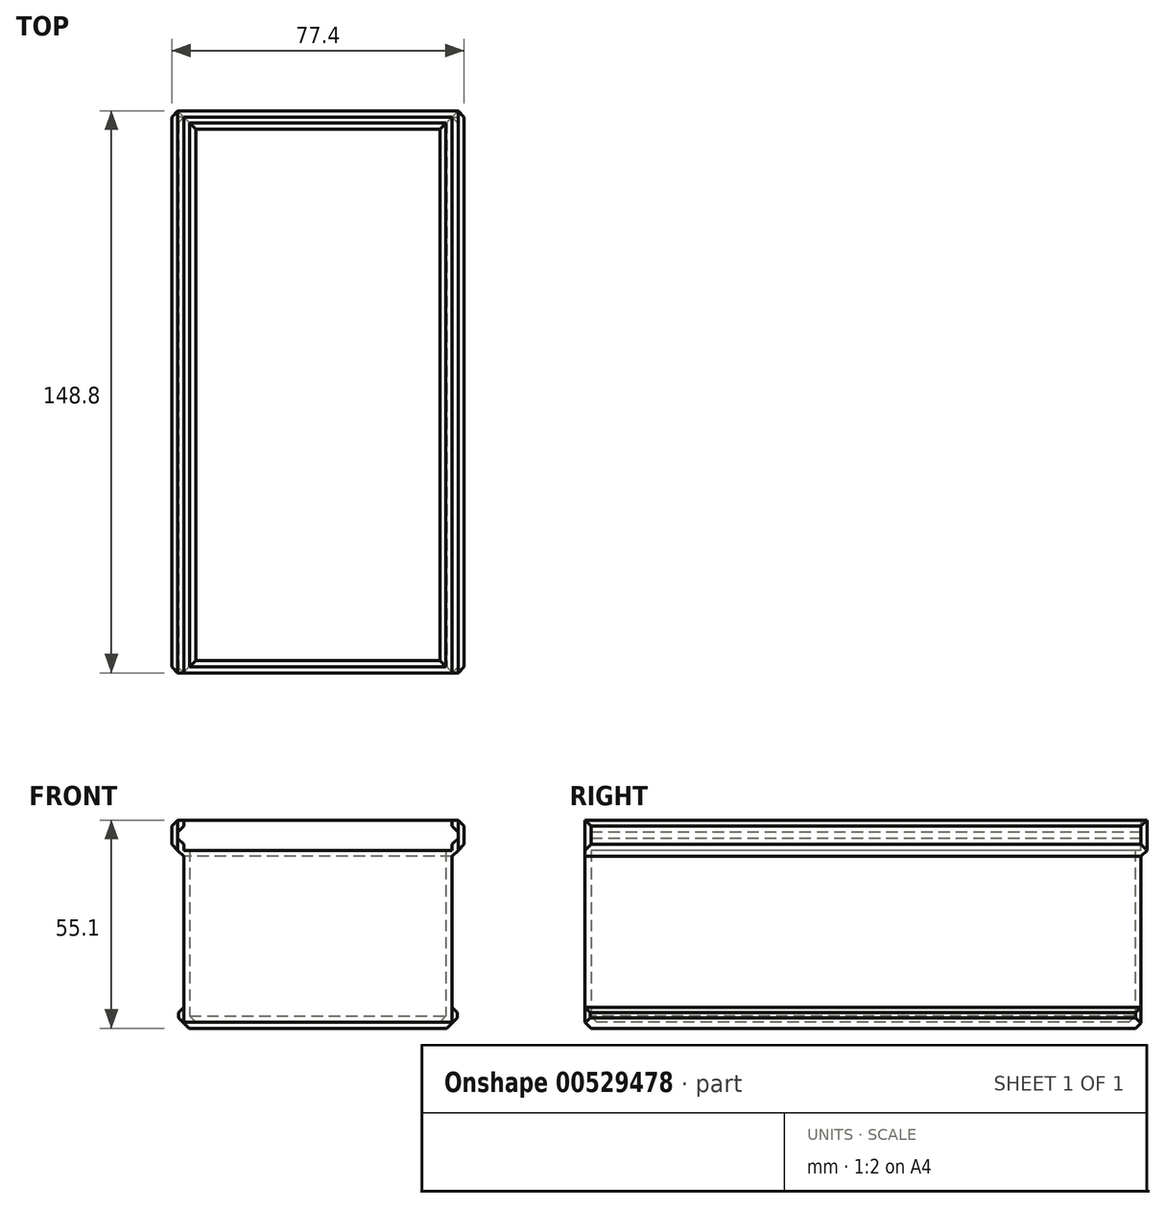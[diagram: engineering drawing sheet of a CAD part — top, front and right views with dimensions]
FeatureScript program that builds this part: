
annotation { "Feature Type Name" : "Feature", "Feature Type Description" : "" }
export const myFeature = defineFeature(function(context is Context, id is Id, definition is map)
    precondition{}
    {
        {
            assignVariable(context, id + "F0", {"name" : "width", "anyValue" : 41.5});
        }
        {
            assignVariable(context, id + "F1", {"name" : "thick", "anyValue" : 1.6});
        }
        {
            assignVariable(context, id + "F2", {"name" : "space", "anyValue" : 4});
        }
        {
            var Q0;
            Q0=qCreatedBy(makeId("Top.planeOp"),FACE);
            var sketch = newSketch(context, id + "F3", { "sketchPlane" : qUnion([Q0])});
            skLineSegment(sketch, "E0.bottom", {"start": v(33.9, 72) * mm, "end": v(-33.9, 72) * mm});
            skLineSegment(sketch, "E0.top", {"start": v(33.9, -72) * mm, "end": v(-33.9, -72) * mm});
            skLineSegment(sketch, "E0.left", {"start": v(33.9, 72) * mm, "end": v(33.9, -72) * mm});
            skLineSegment(sketch, "E0.right", {"start": v(-33.9, 72) * mm, "end": v(-33.9, -72) * mm});
            skPoint(sketch, "E0.middle", {"position": v(0, 0) * mm});
            skSolve(sketch);
        }
        {
            var Q0;
            Q0 = qSketchRegion(id + "F3", true);
            extrude(context, id + "F4", {"entities" : qUnion([Q0]), "depth" : (getVariable(context, 'width') + getVariable(context, 'space')) * mm, "offsetDistance" : 25 * mm});
        }
        {
            var Q0;
            Q0=makeQuery(id+"F4.opExtrude","CAP_FACE",FACE,{"disambiguationData":[OSD([sQuery(id+"F3.wireOp",EDGE,"E0.bottom"),sQuery(id+"F3.wireOp",EDGE,"E0.top"),sQuery(id+"F3.wireOp",EDGE,"E0.left"),sQuery(id+"F3.wireOp",EDGE,"E0.right")])],"isStart":false});
            shell(context, id + "F5", {"entities" : qUnion([Q0]), "thickness" : (getVariable(context, 'thick')) * mm, "oppositeDirection" : true});
        }
        {
            var Q0;
            Q0=makeQuery(id+"F4.opExtrude","SWEPT_FACE",FACE,{"disambiguationData":[OSD([sQuery(id+"F3.wireOp",EDGE,"E0.top")])]});
            var sketch = newSketch(context, id + "F6", { "sketchPlane" : qUnion([Q0])});
            skLineSegment(sketch, "E1", {"start": v(-37.1, 48.7) * mm, "end": v(-37.1, 50.3) * mm});
            skLineSegment(sketch, "E2", {"start": v(-37.1, 50.3) * mm, "end": v(-35.5, 51.9) * mm});
            skLineSegment(sketch, "E3", {"start": v(-35.5, 51.9) * mm, "end": v(-35.5, 53.5) * mm});
            skLineSegment(sketch, "E4", {"start": v(-37.1, 53.5) * mm, "end": v(-38.7, 51.9) * mm});
            skLineSegment(sketch, "E5", {"start": v(-38.7, 51.9) * mm, "end": v(-38.7, 47.1) * mm});
            skLineSegment(sketch, "E6", {"start": v(-37.1, 48.7) * mm, "end": v(-35.5, 47.1) * mm});
            skLineSegment(sketch, "E7", {"start": v(-35.5, 43.9) * mm, "end": v(-38.7, 47.1) * mm});
            skLineSegment(sketch, "E8", {"start": v(-37.1, 53.5) * mm, "end": v(-35.5, 53.5) * mm});
            skLineSegment(sketch, "E9", {"start": v(-35.5, 47.1) * mm, "end": v(-35.5, 45.5) * mm});
            skLineSegment(sketch, "E10", {"start": v(-35.5, 45.5) * mm, "end": v(-35.5, 43.9) * mm});
            skLineSegment(sketch, "E11.MirrorCS", {"start": v(37.1, 50.3) * mm, "end": v(35.5, 51.9) * mm});
            skLineSegment(sketch, "E12.MirrorCS", {"start": v(37.1, 53.5) * mm, "end": v(38.7, 51.9) * mm});
            skLineSegment(sketch, "E13.MirrorCS", {"start": v(35.5, 51.9) * mm, "end": v(35.5, 53.5) * mm});
            skLineSegment(sketch, "E14.MirrorCS", {"start": v(37.1, 48.7) * mm, "end": v(35.5, 47.1) * mm});
            skLineSegment(sketch, "E15.MirrorCS", {"start": v(35.5, 47.1) * mm, "end": v(35.5, 45.5) * mm});
            skLineSegment(sketch, "E16.MirrorCS", {"start": v(37.1, 53.5) * mm, "end": v(35.5, 53.5) * mm});
            skLineSegment(sketch, "E17.MirrorCS", {"start": v(35.5, 45.5) * mm, "end": v(35.5, 43.9) * mm});
            skLineSegment(sketch, "E18.MirrorCS", {"start": v(37.1, 48.7) * mm, "end": v(37.1, 50.3) * mm});
            skLineSegment(sketch, "E19.MirrorCS", {"start": v(38.7, 51.9) * mm, "end": v(38.7, 47.1) * mm});
            skLineSegment(sketch, "E20.MirrorCS", {"start": v(35.5, 43.9) * mm, "end": v(38.7, 47.1) * mm});
            skSolve(sketch);
        }
        {
            var Q0;
            Q0=makeQuery(id+"F6.imprint","IMPRINT",FACE,{"disambiguationData":[TD([[makeQuery(id+"F6.imprint","IMPRINT",EDGE,{"derivedFrom":sQuery(id+"F6.wireOp",EDGE,"E1")}),1.0]])]});
            var Q1;
            Q1=makeQuery(id+"F6.imprint","IMPRINT",FACE,{"disambiguationData":[TD([[makeQuery(id+"F6.imprint","IMPRINT",EDGE,{"derivedFrom":sQuery(id+"F6.wireOp",EDGE,"E11.MirrorCS")}),-1.0]])]});
            var Q2;
            Q2=makeQuery(id+"F4.opExtrude","SWEPT_FACE",FACE,{"disambiguationData":[OSD([sQuery(id+"F3.wireOp",EDGE,"E0.bottom")])]});
            extrude(context, id + "F7", {"entities" : qUnion([Q0, Q1]), "operationType" : NewBodyOperationType.ADD, "endBound" : BoundingType.UP_TO_SURFACE, "oppositeDirection" : true, "depth" : 25 * mm, "endBoundEntityFace" : qUnion([Q2]), "offsetDistance" : 25 * mm});
        }
        {
            var Q0;
            Q0=makeQuery(id+"F4.opExtrude","SWEPT_FACE",FACE,{"disambiguationData":[OSD([sQuery(id+"F3.wireOp",EDGE,"E0.top")])]});
            var sketch = newSketch(context, id + "F8", { "sketchPlane" : qUnion([Q0])});
            skLineSegment(sketch, "E21", {"start": v(-35.5, -0.2) * mm, "end": v(-36.9, 1.2) * mm});
            skLineSegment(sketch, "E22", {"start": v(-36.9, 1.2) * mm, "end": v(-36.9, 2.6) * mm});
            skLineSegment(sketch, "E23", {"start": v(-36.9, 2.6) * mm, "end": v(-35.5, 4) * mm});
            skLineSegment(sketch, "E24.MirrorCS", {"start": v(36.9, 2.6) * mm, "end": v(35.5, 4) * mm});
            skLineSegment(sketch, "E25.MirrorCS", {"start": v(36.9, 1.2) * mm, "end": v(36.9, 2.6) * mm});
            skLineSegment(sketch, "E26.MirrorCS", {"start": v(35.5, -0.2) * mm, "end": v(36.9, 1.2) * mm});
            skLineSegment(sketch, "E27", {"start": v(-35.5, 4) * mm, "end": v(-35.5, -0.2) * mm});
            skLineSegment(sketch, "E28.MirrorCS", {"start": v(35.5, 4) * mm, "end": v(35.5, -0.2) * mm});
            skSolve(sketch);
        }
        {
            var Q0;
            Q0=makeQuery(id+"F8.imprint","IMPRINT",FACE,{"disambiguationData":[TD([[makeQuery(id+"F8.imprint","IMPRINT",EDGE,{"derivedFrom":sQuery(id+"F8.wireOp",EDGE,"E21")}),-1.0]])]});
            var Q1;
            Q1=makeQuery(id+"F8.imprint","IMPRINT",FACE,{"disambiguationData":[TD([[makeQuery(id+"F8.imprint","IMPRINT",EDGE,{"derivedFrom":sQuery(id+"F8.wireOp",EDGE,"E24.MirrorCS")}),1.0]])]});
            var Q2;
            Q2=makeQuery(id+"F7.boolean.opBoolean","MERGE",FACE,{"derivedFrom":[makeQuery(id+"F4.opExtrude","SWEPT_FACE",FACE,{"disambiguationData":[OSD([sQuery(id+"F3.wireOp",EDGE,"E0.bottom")])]}),makeQuery(id+"F7.opExtrude","CAP_FACE",FACE,{"disambiguationData":[OSD([sQuery(id+"F6.wireOp",EDGE,"E1"),sQuery(id+"F6.wireOp",EDGE,"E2"),sQuery(id+"F6.wireOp",EDGE,"E3"),sQuery(id+"F6.wireOp",EDGE,"E4"),sQuery(id+"F6.wireOp",EDGE,"E5"),sQuery(id+"F6.wireOp",EDGE,"E6"),sQuery(id+"F6.wireOp",EDGE,"E7"),sQuery(id+"F6.wireOp",EDGE,"E8"),sQuery(id+"F6.wireOp",EDGE,"E9"),sQuery(id+"F6.wireOp",EDGE,"E10")])],"isStart":false}),makeQuery(id+"F7.opExtrude","CAP_FACE",FACE,{"disambiguationData":[OSD([sQuery(id+"F6.wireOp",EDGE,"E11.MirrorCS"),sQuery(id+"F6.wireOp",EDGE,"E12.MirrorCS"),sQuery(id+"F6.wireOp",EDGE,"E13.MirrorCS"),sQuery(id+"F6.wireOp",EDGE,"E14.MirrorCS"),sQuery(id+"F6.wireOp",EDGE,"E15.MirrorCS"),sQuery(id+"F6.wireOp",EDGE,"E16.MirrorCS"),sQuery(id+"F6.wireOp",EDGE,"E17.MirrorCS"),sQuery(id+"F6.wireOp",EDGE,"E18.MirrorCS"),sQuery(id+"F6.wireOp",EDGE,"E19.MirrorCS"),sQuery(id+"F6.wireOp",EDGE,"E20.MirrorCS")])],"isStart":false})]});
            extrude(context, id + "F9", {"entities" : qUnion([Q0, Q1]), "operationType" : NewBodyOperationType.ADD, "endBound" : BoundingType.UP_TO_SURFACE, "oppositeDirection" : true, "depth" : 25 * mm, "endBoundEntityFace" : qUnion([Q2]), "offsetDistance" : .4 * mm});
        }
        {
            var Q0;
            Q0=makeQuery(id+"F4.opExtrude","CAP_EDGE",EDGE,{"disambiguationData":[OSD([sQuery(id+"F3.wireOp",EDGE,"E0.right")])],"isStart":false});
            var Q1;
            Q1=makeQuery(id+"F4.opExtrude","CAP_EDGE",EDGE,{"disambiguationData":[OSD([sQuery(id+"F3.wireOp",EDGE,"E0.left")])],"isStart":false});
            var Q2;
            {var subQ0=sQuery(id+"F3.wireOp",EDGE,"E0.right");Q2=makeQuery(id+"F5.opShell","OFFSET_EDGE",EDGE,{"disambiguationData":[OSD([subQ0]),TDD([makeQuery(id+"F4.opExtrude","CAP_EDGE",EDGE,{"disambiguationData":[OSD([subQ0])],"isStart":true})])]});}
            var Q3;
            {var subQ0=sQuery(id+"F3.wireOp",EDGE,"E0.left");Q3=makeQuery(id+"F5.opShell","OFFSET_EDGE",EDGE,{"disambiguationData":[OSD([subQ0]),TDD([makeQuery(id+"F4.opExtrude","CAP_EDGE",EDGE,{"disambiguationData":[OSD([subQ0])],"isStart":true})])]});}
            var Q4;
            {var subQ0=sQuery(id+"F3.wireOp",EDGE,"E0.bottom");Q4=makeQuery(id+"F5.opShell","OFFSET_EDGE",EDGE,{"disambiguationData":[OSD([subQ0]),TDD([makeQuery(id+"F4.opExtrude","CAP_EDGE",EDGE,{"disambiguationData":[OSD([subQ0])],"isStart":true})])]});}
            var Q5;
            {var subQ0=sQuery(id+"F3.wireOp",EDGE,"E0.top");Q5=makeQuery(id+"F5.opShell","OFFSET_EDGE",EDGE,{"disambiguationData":[OSD([subQ0]),TDD([makeQuery(id+"F4.opExtrude","CAP_EDGE",EDGE,{"disambiguationData":[OSD([subQ0])],"isStart":true})])]});}
            chamfer(context, id + "F10", {"entities" : qUnion([Q0, Q1, Q2, Q3, Q4, Q5]), "width" : (getVariable(context, 'thick')) * mm, "tangentPropagation" : true});
        }
        {
            var Q0;
            Q0=makeQuery(id+"F4.opExtrude","CAP_EDGE",EDGE,{"disambiguationData":[OSD([sQuery(id+"F3.wireOp",EDGE,"E0.right")])],"isStart":true});
            var Q1;
            Q1=makeQuery(id+"F4.opExtrude","CAP_EDGE",EDGE,{"disambiguationData":[OSD([sQuery(id+"F3.wireOp",EDGE,"E0.left")])],"isStart":true});
            var Q2;
            Q2=makeQuery(id+"F9.opExtrude","CAP_EDGE",EDGE,{"disambiguationData":[OSD([sQuery(id+"F8.wireOp",EDGE,"E22")])],"isStart":true});
            var Q3;
            Q3=makeQuery(id+"F9.opExtrude","CAP_EDGE",EDGE,{"disambiguationData":[OSD([sQuery(id+"F8.wireOp",EDGE,"E25.MirrorCS")])],"isStart":true});
            var Q4;
            Q4=makeQuery(id+"F9.opExtrude","CAP_EDGE",EDGE,{"disambiguationData":[OSD([sQuery(id+"F8.wireOp",EDGE,"E22")])],"isStart":false});
            var Q5;
            Q5=makeQuery(id+"F9.opExtrude","CAP_EDGE",EDGE,{"disambiguationData":[OSD([sQuery(id+"F8.wireOp",EDGE,"E25.MirrorCS")])],"isStart":false});
            var Q6;
            Q6=makeQuery(id+"F4.opExtrude","CAP_EDGE",EDGE,{"disambiguationData":[OSD([sQuery(id+"F3.wireOp",EDGE,"E0.bottom")])],"isStart":true});
            chamfer(context, id + "F11", {"entities" : qUnion([Q0, Q1, Q2, Q3, Q4, Q5, Q6]), "width" : (getVariable(context, 'thick') - .2) * mm, "tangentPropagation" : true});
        }
        {
            var Q0;
            Q0=makeQuery(id+"F9.boolean.opBoolean","MERGE",FACE,{"derivedFrom":[makeQuery(id+"F7.boolean.opBoolean","MERGE",FACE,{"derivedFrom":[makeQuery(id+"F4.opExtrude","SWEPT_FACE",FACE,{"disambiguationData":[OSD([sQuery(id+"F3.wireOp",EDGE,"E0.bottom")])]}),makeQuery(id+"F7.opExtrude","CAP_FACE",FACE,{"disambiguationData":[OSD([sQuery(id+"F6.wireOp",EDGE,"E1"),sQuery(id+"F6.wireOp",EDGE,"E2"),sQuery(id+"F6.wireOp",EDGE,"E3"),sQuery(id+"F6.wireOp",EDGE,"E4"),sQuery(id+"F6.wireOp",EDGE,"E5"),sQuery(id+"F6.wireOp",EDGE,"E6"),sQuery(id+"F6.wireOp",EDGE,"E7"),sQuery(id+"F6.wireOp",EDGE,"E8"),sQuery(id+"F6.wireOp",EDGE,"E9"),sQuery(id+"F6.wireOp",EDGE,"E10")])],"isStart":false}),makeQuery(id+"F7.opExtrude","CAP_FACE",FACE,{"disambiguationData":[OSD([sQuery(id+"F6.wireOp",EDGE,"E11.MirrorCS"),sQuery(id+"F6.wireOp",EDGE,"E12.MirrorCS"),sQuery(id+"F6.wireOp",EDGE,"E13.MirrorCS"),sQuery(id+"F6.wireOp",EDGE,"E14.MirrorCS"),sQuery(id+"F6.wireOp",EDGE,"E15.MirrorCS"),sQuery(id+"F6.wireOp",EDGE,"E16.MirrorCS"),sQuery(id+"F6.wireOp",EDGE,"E17.MirrorCS"),sQuery(id+"F6.wireOp",EDGE,"E18.MirrorCS"),sQuery(id+"F6.wireOp",EDGE,"E19.MirrorCS"),sQuery(id+"F6.wireOp",EDGE,"E20.MirrorCS")])],"isStart":false})]}),makeQuery(id+"F9.opExtrude","CAP_FACE",FACE,{"disambiguationData":[OSD([sQuery(id+"F8.wireOp",EDGE,"E21"),sQuery(id+"F8.wireOp",EDGE,"E22"),sQuery(id+"F8.wireOp",EDGE,"E23"),sQuery(id+"F8.wireOp",EDGE,"E27")])],"isStart":false}),makeQuery(id+"F9.opExtrude","CAP_FACE",FACE,{"disambiguationData":[OSD([sQuery(id+"F8.wireOp",EDGE,"E24.MirrorCS"),sQuery(id+"F8.wireOp",EDGE,"E25.MirrorCS"),sQuery(id+"F8.wireOp",EDGE,"E26.MirrorCS"),sQuery(id+"F8.wireOp",EDGE,"E28.MirrorCS")])],"isStart":false})]});
            var sketch = newSketch(context, id + "F12", { "sketchPlane" : qUnion([Q0])});
            skLineSegment(sketch, "E29", {"start": v(-35.5, 43.9) * mm, "end": v(35.5, 43.9) * mm});
            skLineSegment(sketch, "E30", {"start": v(-35.5, 53.5) * mm, "end": v(35.5, 53.5) * mm});
            skSolve(sketch);
        }
        {
            var Q0;
            Q0=makeQuery(id+"F12.imprint","IMPRINT",FACE,{"disambiguationData":[TD([[makeQuery(id+"F12.imprint","IMPRINT",EDGE,{"derivedFrom":sQuery(id+"F12.wireOp",EDGE,"E30")}),-1.0]])]});
            var Q1;
            Q1=makeQuery(id+"F12.imprint","IMPRINT",FACE,{"disambiguationData":[TD([[makeQuery(id+"F12.imprint","IMPRINT",EDGE,{"derivedFrom":sQuery(id+"F12.wireOp",EDGE,"E29")}),1.0]])]});
            extrude(context, id + "F13", {"entities" : qUnion([Q0, Q1]), "operationType" : NewBodyOperationType.ADD, "depth" : (getVariable(context, 'thick')) * mm, "offsetDistance" : 25 * mm});
        }
        {
            var Q0;
            Q0=makeQuery(id+"F13.opExtrude","CAP_EDGE",EDGE,{"disambiguationData":[OSD([sQuery(id+"F3.wireOp",EDGE,"E0.bottom"),sQuery(id+"F6.wireOp",EDGE,"E5")])],"isStart":false});
            var Q1;
            Q1=makeQuery(id+"F13.opExtrude","CAP_EDGE",EDGE,{"disambiguationData":[OSD([sQuery(id+"F3.wireOp",EDGE,"E0.bottom"),sQuery(id+"F6.wireOp",EDGE,"E19.MirrorCS")])],"isStart":false});
            var Q2;
            Q2=makeQuery(id+"F7.opExtrude","CAP_EDGE",EDGE,{"disambiguationData":[OSD([sQuery(id+"F6.wireOp",EDGE,"E1")])],"isStart":false});
            var Q3;
            Q3=makeQuery(id+"F4.opExtrude","CAP_EDGE",EDGE,{"disambiguationData":[OSD([sQuery(id+"F3.wireOp",EDGE,"E0.bottom")])],"isStart":false});
            var Q4;
            Q4=makeQuery(id+"F13.opExtrude","CAP_EDGE",EDGE,{"disambiguationData":[OSD([sQuery(id+"F12.wireOp",EDGE,"E29")])],"isStart":false});
            var Q5;
            Q5=makeQuery(id+"F4.opExtrude","CAP_EDGE",EDGE,{"disambiguationData":[OSD([sQuery(id+"F3.wireOp",EDGE,"E0.top")])],"isStart":true});
            var Q6;
            Q6=makeQuery(id+"F7.opExtrude","CAP_EDGE",EDGE,{"disambiguationData":[OSD([sQuery(id+"F6.wireOp",EDGE,"E5")])],"isStart":true});
            var Q7;
            Q7=makeQuery(id+"F7.opExtrude","CAP_EDGE",EDGE,{"disambiguationData":[OSD([sQuery(id+"F6.wireOp",EDGE,"E19.MirrorCS")])],"isStart":true});
            chamfer(context, id + "F14", {"entities" : qUnion([Q0, Q1, Q2, Q3, Q4, Q5, Q6, Q7]), "width" : (getVariable(context, 'thick')) * mm, "tangentPropagation" : true});
        }
    });
